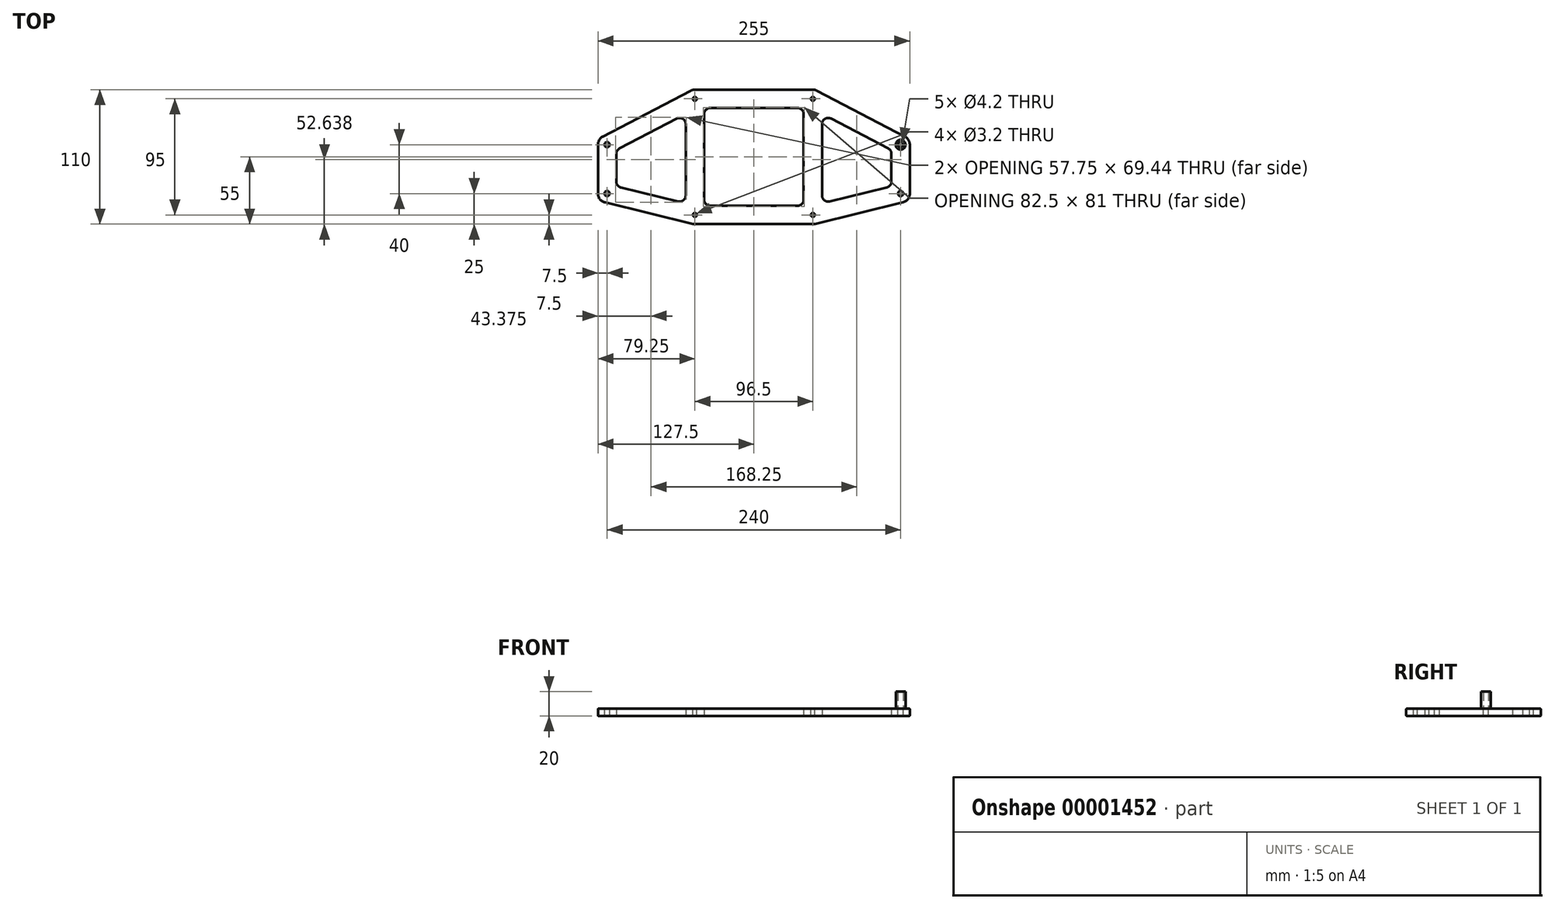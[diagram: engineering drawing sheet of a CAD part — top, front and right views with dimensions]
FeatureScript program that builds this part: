
annotation { "Feature Type Name" : "Feature", "Feature Type Description" : "" }
export const myFeature = defineFeature(function(context is Context, id is Id, definition is map)
    precondition{}
    {
        {
            var Q0;
            Q0=qCreatedBy(makeId("Top.planeOp"),FACE);
            var sketch = newSketch(context, id + "F0", { "sketchPlane" : qUnion([Q0])});
            skLineSegment(sketch, "E0.rect.bottom", {"start": v(120, 20) * mm, "end": v(-120, 20) * mm, "construction": true});
            skLineSegment(sketch, "E0.rect.top", {"start": v(120, -20) * mm, "end": v(-120, -20) * mm, "construction": true});
            skLineSegment(sketch, "E0.rect.left", {"start": v(120, 20) * mm, "end": v(120, -20) * mm, "construction": true});
            skLineSegment(sketch, "E0.rect.right", {"start": v(-120, 20) * mm, "end": v(-120, -20) * mm, "construction": true});
            skPoint(sketch, "E0.rect.middle", {"position": v(0, 0) * mm});
            skLineSegment(sketch, "E1.rect.bottom", {"start": v(48.25, 57.5) * mm, "end": v(-48.25, 57.5) * mm, "construction": true});
            skLineSegment(sketch, "E1.rect.top", {"start": v(48.25, -37.5) * mm, "end": v(-48.25, -37.5) * mm, "construction": true});
            skLineSegment(sketch, "E1.rect.left", {"start": v(48.25, 57.5) * mm, "end": v(48.25, -37.5) * mm, "construction": true});
            skLineSegment(sketch, "E1.rect.right", {"start": v(-48.25, 57.5) * mm, "end": v(-48.25, -37.5) * mm, "construction": true});
            skPoint(sketch, "E1.rect.middle", {"position": v(0, 10) * mm});
            skLineSegment(sketch, "E2", {"start": v(-120, 20) * mm, "end": v(-48.25, 57.5) * mm, "construction": true});
            skLineSegment(sketch, "E3", {"start": v(48.25, 57.5) * mm, "end": v(120, 20) * mm, "construction": true});
            skLineSegment(sketch, "E4", {"start": v(120, -20) * mm, "end": v(48.25, -37.5) * mm, "construction": true});
            skLineSegment(sketch, "E5", {"start": v(-48.25, -37.5) * mm, "end": v(-120, -20) * mm, "construction": true});
            skLineSegment(sketch, "E6.0", {"start": v(-127.5, 24.54) * mm, "end": v(-127.5, -25.9) * mm});
            skLineSegment(sketch, "E6.1", {"start": v(-49.15, -45) * mm, "end": v(-127.5, -25.9) * mm});
            skLineSegment(sketch, "E6.2", {"start": v(49.15, -45) * mm, "end": v(-49.15, -45) * mm});
            skLineSegment(sketch, "E6.3", {"start": v(127.5, -25.9) * mm, "end": v(49.15, -45) * mm});
            skLineSegment(sketch, "E6.4", {"start": v(127.5, 24.54) * mm, "end": v(127.5, -25.9) * mm});
            skLineSegment(sketch, "E6.5", {"start": v(-127.5, 24.54) * mm, "end": v(-50.1, 65) * mm});
            skLineSegment(sketch, "E6.6", {"start": v(50.1, 65) * mm, "end": v(127.5, 24.54) * mm});
            skLineSegment(sketch, "E6.7", {"start": v(50.1, 65) * mm, "end": v(-50.1, 65) * mm});
            skLineSegment(sketch, "E7.0", {"start": v(-112.5, 15.46) * mm, "end": v(-55.75, 45.12) * mm});
            skLineSegment(sketch, "E7.1", {"start": v(-112.5, 15.46) * mm, "end": v(-112.5, -14.1) * mm});
            skLineSegment(sketch, "E7.2", {"start": v(-55.75, -27.95) * mm, "end": v(-112.5, -14.1) * mm});
            skLineSegment(sketch, "E7.3", {"start": v(-55.75, 45.12) * mm, "end": v(-55.75, -27.95) * mm});
            skLineSegment(sketch, "E8.0", {"start": v(-40.75, 50) * mm, "end": v(-40.75, -30) * mm});
            skLineSegment(sketch, "E8.1", {"start": v(40.75, 50) * mm, "end": v(-40.75, 50) * mm});
            skLineSegment(sketch, "E8.2", {"start": v(40.75, 50) * mm, "end": v(40.75, -30) * mm});
            skLineSegment(sketch, "E8.3", {"start": v(40.75, -30) * mm, "end": v(-40.75, -30) * mm});
            skLineSegment(sketch, "E9.0", {"start": v(55.75, 45.12) * mm, "end": v(112.5, 15.46) * mm});
            skLineSegment(sketch, "E9.1", {"start": v(55.75, 45.12) * mm, "end": v(55.75, -27.95) * mm});
            skLineSegment(sketch, "E9.2", {"start": v(112.5, -14.1) * mm, "end": v(55.75, -27.95) * mm});
            skLineSegment(sketch, "E9.3", {"start": v(112.5, 15.46) * mm, "end": v(112.5, -14.1) * mm});
            skSolve(sketch);
        }
        {
            var Q0;
            Q0=makeQuery(id+"F0.imprint","IMPRINT",FACE,{"disambiguationData":[TD([[makeQuery(id+"F0.imprint","IMPRINT",EDGE,{"derivedFrom":sQuery(id+"F0.wireOp",EDGE,"E6.0")}),1.0]])]});
            extrude(context, id + "F1", {"entities" : qUnion([Q0]), "depth" : 6 * mm});
        }
        {
            var Q0;
            Q0=makeQuery(id+"F1.opExtrude","SWEPT_EDGE",EDGE,{"disambiguationData":[OSD([sQuery(id+"F0.wireOp",EDGE,"E6.0"),sQuery(id+"F0.wireOp",EDGE,"E6.1")])]});
            var Q1;
            Q1=makeQuery(id+"F1.opExtrude","SWEPT_EDGE",EDGE,{"disambiguationData":[OSD([sQuery(id+"F0.wireOp",EDGE,"E6.0"),sQuery(id+"F0.wireOp",EDGE,"E6.5")])]});
            var Q2;
            Q2=makeQuery(id+"F1.opExtrude","SWEPT_EDGE",EDGE,{"disambiguationData":[OSD([sQuery(id+"F0.wireOp",EDGE,"E6.1"),sQuery(id+"F0.wireOp",EDGE,"E6.2")])]});
            var Q3;
            Q3=makeQuery(id+"F1.opExtrude","SWEPT_EDGE",EDGE,{"disambiguationData":[OSD([sQuery(id+"F0.wireOp",EDGE,"E6.2"),sQuery(id+"F0.wireOp",EDGE,"E6.3")])]});
            var Q4;
            Q4=makeQuery(id+"F1.opExtrude","SWEPT_EDGE",EDGE,{"disambiguationData":[OSD([sQuery(id+"F0.wireOp",EDGE,"E6.3"),sQuery(id+"F0.wireOp",EDGE,"E6.4")])]});
            var Q5;
            Q5=makeQuery(id+"F1.opExtrude","SWEPT_EDGE",EDGE,{"disambiguationData":[OSD([sQuery(id+"F0.wireOp",EDGE,"E6.4"),sQuery(id+"F0.wireOp",EDGE,"E6.6")])]});
            var Q6;
            Q6=makeQuery(id+"F1.opExtrude","SWEPT_EDGE",EDGE,{"disambiguationData":[OSD([sQuery(id+"F0.wireOp",EDGE,"E6.6"),sQuery(id+"F0.wireOp",EDGE,"E6.7")])]});
            var Q7;
            Q7=makeQuery(id+"F1.opExtrude","SWEPT_EDGE",EDGE,{"disambiguationData":[OSD([sQuery(id+"F0.wireOp",EDGE,"E6.5"),sQuery(id+"F0.wireOp",EDGE,"E6.7")])]});
            fillet(context, id + "F2", {"entities" : qUnion([Q0, Q1, Q2, Q3, Q4, Q5, Q6, Q7]), "radius" : 7.5 * mm, "tangentPropagation" : true, "allowEdgeOverflow" : false});
        }
        {
            var Q0;
            Q0=makeQuery(id+"F1.opExtrude","SWEPT_EDGE",EDGE,{"disambiguationData":[OSD([sQuery(id+"F0.wireOp",EDGE,"E7.0"),sQuery(id+"F0.wireOp",EDGE,"E7.1")])]});
            var Q1;
            Q1=makeQuery(id+"F1.opExtrude","SWEPT_EDGE",EDGE,{"disambiguationData":[OSD([sQuery(id+"F0.wireOp",EDGE,"E7.1"),sQuery(id+"F0.wireOp",EDGE,"E7.2")])]});
            var Q2;
            Q2=makeQuery(id+"F1.opExtrude","SWEPT_EDGE",EDGE,{"disambiguationData":[OSD([sQuery(id+"F0.wireOp",EDGE,"E7.2"),sQuery(id+"F0.wireOp",EDGE,"E7.3")])]});
            var Q3;
            Q3=makeQuery(id+"F1.opExtrude","SWEPT_EDGE",EDGE,{"disambiguationData":[OSD([sQuery(id+"F0.wireOp",EDGE,"E7.0"),sQuery(id+"F0.wireOp",EDGE,"E7.3")])]});
            var Q4;
            Q4=makeQuery(id+"F1.opExtrude","SWEPT_EDGE",EDGE,{"disambiguationData":[OSD([sQuery(id+"F0.wireOp",EDGE,"E8.0"),sQuery(id+"F0.wireOp",EDGE,"E8.1")])]});
            var Q5;
            Q5=makeQuery(id+"F1.opExtrude","SWEPT_EDGE",EDGE,{"disambiguationData":[OSD([sQuery(id+"F0.wireOp",EDGE,"E8.0"),sQuery(id+"F0.wireOp",EDGE,"E8.3")])]});
            var Q6;
            Q6=makeQuery(id+"F1.opExtrude","SWEPT_EDGE",EDGE,{"disambiguationData":[OSD([sQuery(id+"F0.wireOp",EDGE,"E8.2"),sQuery(id+"F0.wireOp",EDGE,"E8.3")])]});
            var Q7;
            Q7=makeQuery(id+"F1.opExtrude","SWEPT_EDGE",EDGE,{"disambiguationData":[OSD([sQuery(id+"F0.wireOp",EDGE,"E8.1"),sQuery(id+"F0.wireOp",EDGE,"E8.2")])]});
            var Q8;
            Q8=makeQuery(id+"F1.opExtrude","SWEPT_EDGE",EDGE,{"disambiguationData":[OSD([sQuery(id+"F0.wireOp",EDGE,"E9.1"),sQuery(id+"F0.wireOp",EDGE,"E9.2")])]});
            var Q9;
            Q9=makeQuery(id+"F1.opExtrude","SWEPT_EDGE",EDGE,{"disambiguationData":[OSD([sQuery(id+"F0.wireOp",EDGE,"E9.0"),sQuery(id+"F0.wireOp",EDGE,"E9.3")])]});
            var Q10;
            Q10=makeQuery(id+"F1.opExtrude","SWEPT_EDGE",EDGE,{"disambiguationData":[OSD([sQuery(id+"F0.wireOp",EDGE,"E9.2"),sQuery(id+"F0.wireOp",EDGE,"E9.3")])]});
            var Q11;
            Q11=makeQuery(id+"F1.opExtrude","SWEPT_EDGE",EDGE,{"disambiguationData":[OSD([sQuery(id+"F0.wireOp",EDGE,"E9.0"),sQuery(id+"F0.wireOp",EDGE,"E9.1")])]});
            fillet(context, id + "F3", {"entities" : qUnion([Q0, Q1, Q2, Q3, Q4, Q5, Q6, Q7, Q8, Q9, Q10, Q11]), "radius" : 5 * mm, "tangentPropagation" : true, "allowEdgeOverflow" : false});
        }
        {
            var Q0;
            Q0=makeQuery(id+"F1.opExtrude","CAP_FACE",FACE,{"disambiguationData":[OSD([sQuery(id+"F0.wireOp",EDGE,"E6.0"),sQuery(id+"F0.wireOp",EDGE,"E6.1"),sQuery(id+"F0.wireOp",EDGE,"E6.2"),sQuery(id+"F0.wireOp",EDGE,"E6.3"),sQuery(id+"F0.wireOp",EDGE,"E6.4"),sQuery(id+"F0.wireOp",EDGE,"E6.5"),sQuery(id+"F0.wireOp",EDGE,"E6.6"),sQuery(id+"F0.wireOp",EDGE,"E6.7"),sQuery(id+"F0.wireOp",EDGE,"E7.0"),sQuery(id+"F0.wireOp",EDGE,"E7.1"),sQuery(id+"F0.wireOp",EDGE,"E7.2"),sQuery(id+"F0.wireOp",EDGE,"E7.3"),sQuery(id+"F0.wireOp",EDGE,"E8.0"),sQuery(id+"F0.wireOp",EDGE,"E8.1"),sQuery(id+"F0.wireOp",EDGE,"E8.2"),sQuery(id+"F0.wireOp",EDGE,"E8.3"),sQuery(id+"F0.wireOp",EDGE,"E9.0"),sQuery(id+"F0.wireOp",EDGE,"E9.1"),sQuery(id+"F0.wireOp",EDGE,"E9.2"),sQuery(id+"F0.wireOp",EDGE,"E9.3")])],"isStart":false});
            var Q1;
            Q1=makeQuery(id+"F1.opExtrude","CAP_FACE",FACE,{"disambiguationData":[OSD([sQuery(id+"F0.wireOp",EDGE,"E6.0"),sQuery(id+"F0.wireOp",EDGE,"E6.1"),sQuery(id+"F0.wireOp",EDGE,"E6.2"),sQuery(id+"F0.wireOp",EDGE,"E6.3"),sQuery(id+"F0.wireOp",EDGE,"E6.4"),sQuery(id+"F0.wireOp",EDGE,"E6.5"),sQuery(id+"F0.wireOp",EDGE,"E6.6"),sQuery(id+"F0.wireOp",EDGE,"E6.7"),sQuery(id+"F0.wireOp",EDGE,"E7.0"),sQuery(id+"F0.wireOp",EDGE,"E7.1"),sQuery(id+"F0.wireOp",EDGE,"E7.2"),sQuery(id+"F0.wireOp",EDGE,"E7.3"),sQuery(id+"F0.wireOp",EDGE,"E8.0"),sQuery(id+"F0.wireOp",EDGE,"E8.1"),sQuery(id+"F0.wireOp",EDGE,"E8.2"),sQuery(id+"F0.wireOp",EDGE,"E8.3"),sQuery(id+"F0.wireOp",EDGE,"E9.0"),sQuery(id+"F0.wireOp",EDGE,"E9.1"),sQuery(id+"F0.wireOp",EDGE,"E9.2"),sQuery(id+"F0.wireOp",EDGE,"E9.3")])],"isStart":true});
            fillet(context, id + "F4", {"entities" : qUnion([Q0, Q1]), "radius" : .5 * mm, "tangentPropagation" : true, "allowEdgeOverflow" : false});
        }
        {
            var Q0;
            Q0=makeQuery(id+"F1.opExtrude","CAP_FACE",FACE,{"disambiguationData":[OSD([sQuery(id+"F0.wireOp",EDGE,"E6.0"),sQuery(id+"F0.wireOp",EDGE,"E6.1"),sQuery(id+"F0.wireOp",EDGE,"E6.2"),sQuery(id+"F0.wireOp",EDGE,"E6.3"),sQuery(id+"F0.wireOp",EDGE,"E6.4"),sQuery(id+"F0.wireOp",EDGE,"E6.5"),sQuery(id+"F0.wireOp",EDGE,"E6.6"),sQuery(id+"F0.wireOp",EDGE,"E6.7"),sQuery(id+"F0.wireOp",EDGE,"E7.0"),sQuery(id+"F0.wireOp",EDGE,"E7.1"),sQuery(id+"F0.wireOp",EDGE,"E7.2"),sQuery(id+"F0.wireOp",EDGE,"E7.3"),sQuery(id+"F0.wireOp",EDGE,"E8.0"),sQuery(id+"F0.wireOp",EDGE,"E8.1"),sQuery(id+"F0.wireOp",EDGE,"E8.2"),sQuery(id+"F0.wireOp",EDGE,"E8.3"),sQuery(id+"F0.wireOp",EDGE,"E9.0"),sQuery(id+"F0.wireOp",EDGE,"E9.1"),sQuery(id+"F0.wireOp",EDGE,"E9.2"),sQuery(id+"F0.wireOp",EDGE,"E9.3")])],"isStart":false});
            var sketch = newSketch(context, id + "F5", { "sketchPlane" : qUnion([Q0])});
            skLineSegment(sketch, "E10.rect.bottom", {"start": v(120, 20) * mm, "end": v(-120, 20) * mm, "construction": true});
            skLineSegment(sketch, "E10.rect.top", {"start": v(120, -20) * mm, "end": v(-120, -20) * mm, "construction": true});
            skLineSegment(sketch, "E10.rect.left", {"start": v(120, 20) * mm, "end": v(120, -20) * mm, "construction": true});
            skLineSegment(sketch, "E10.rect.right", {"start": v(-120, 20) * mm, "end": v(-120, -20) * mm, "construction": true});
            skPoint(sketch, "E10.rect.middle", {"position": v(0, 0) * mm});
            skLineSegment(sketch, "E11.rect.bottom", {"start": v(-48.25, 57.5) * mm, "end": v(48.25, 57.5) * mm, "construction": true});
            skLineSegment(sketch, "E11.rect.top", {"start": v(-48.25, -37.5) * mm, "end": v(48.25, -37.5) * mm, "construction": true});
            skLineSegment(sketch, "E11.rect.left", {"start": v(-48.25, 57.5) * mm, "end": v(-48.25, -37.5) * mm, "construction": true});
            skLineSegment(sketch, "E11.rect.right", {"start": v(48.25, 57.5) * mm, "end": v(48.25, -37.5) * mm, "construction": true});
            skPoint(sketch, "E11.rect.middle", {"position": v(0, 10) * mm});
            skCircle(sketch, "E12", {"center": v(-120, 20) * mm, "radius": 2.1 * mm});
            skCircle(sketch, "E13", {"center": v(-48.25, 57.5) * mm, "radius": 1.6 * mm});
            skCircle(sketch, "E14", {"center": v(48.25, 57.5) * mm, "radius": 1.6 * mm});
            skCircle(sketch, "E15", {"center": v(120, 20) * mm, "radius": 2.1 * mm});
            skCircle(sketch, "E16", {"center": v(120, -20) * mm, "radius": 2.1 * mm});
            skCircle(sketch, "E17", {"center": v(48.25, -37.5) * mm, "radius": 1.6 * mm});
            skCircle(sketch, "E18", {"center": v(-48.25, -37.5) * mm, "radius": 1.6 * mm});
            skCircle(sketch, "E19", {"center": v(-120, -20) * mm, "radius": 2.1 * mm});
            skSolve(sketch);
        }
        {
            var Q0;
            {Q0=qUnion([makeQuery(id+"F5.imprint","IMPRINT",FACE,{"disambiguationData":[TD([[makeQuery(id+"F5.imprint","IMPRINT",EDGE,{"derivedFrom":sQuery(id+"F5.wireOp",EDGE,"E12")}),1.0]])]}),makeQuery(id+"F5.imprint","IMPRINT",FACE,{"disambiguationData":[TD([[makeQuery(id+"F5.imprint","IMPRINT",EDGE,{"derivedFrom":sQuery(id+"F5.wireOp",EDGE,"E13")}),1.0]])]}),makeQuery(id+"F5.imprint","IMPRINT",FACE,{"disambiguationData":[TD([[makeQuery(id+"F5.imprint","IMPRINT",EDGE,{"derivedFrom":sQuery(id+"F5.wireOp",EDGE,"E14")}),1.0]])]}),makeQuery(id+"F5.imprint","IMPRINT",FACE,{"disambiguationData":[TD([[makeQuery(id+"F5.imprint","IMPRINT",EDGE,{"derivedFrom":sQuery(id+"F5.wireOp",EDGE,"E15")}),1.0]])]}),makeQuery(id+"F5.imprint","IMPRINT",FACE,{"disambiguationData":[TD([[makeQuery(id+"F5.imprint","IMPRINT",EDGE,{"derivedFrom":sQuery(id+"F5.wireOp",EDGE,"E16")}),1.0]])]}),makeQuery(id+"F5.imprint","IMPRINT",FACE,{"disambiguationData":[TD([[makeQuery(id+"F5.imprint","IMPRINT",EDGE,{"derivedFrom":sQuery(id+"F5.wireOp",EDGE,"E17")}),1.0]])]}),makeQuery(id+"F5.imprint","IMPRINT",FACE,{"disambiguationData":[TD([[makeQuery(id+"F5.imprint","IMPRINT",EDGE,{"derivedFrom":sQuery(id+"F5.wireOp",EDGE,"E18")}),1.0]])]}),makeQuery(id+"F5.imprint","IMPRINT",FACE,{"disambiguationData":[TD([[makeQuery(id+"F5.imprint","IMPRINT",EDGE,{"derivedFrom":sQuery(id+"F5.wireOp",EDGE,"E19")}),1.0]])]})]);}
            extrude(context, id + "F6", {"entities" : qUnion([Q0]), "operationType" : NewBodyOperationType.REMOVE, "endBound" : BoundingType.THROUGH_ALL, "oppositeDirection" : true, "depth" : 25 * mm});
        }
        {
            var Q0;
            Q0=makeQuery(id+"F1.opExtrude","CAP_FACE",FACE,{"disambiguationData":[OSD([sQuery(id+"F0.wireOp",EDGE,"E6.0"),sQuery(id+"F0.wireOp",EDGE,"E6.1"),sQuery(id+"F0.wireOp",EDGE,"E6.2"),sQuery(id+"F0.wireOp",EDGE,"E6.3"),sQuery(id+"F0.wireOp",EDGE,"E6.4"),sQuery(id+"F0.wireOp",EDGE,"E6.5"),sQuery(id+"F0.wireOp",EDGE,"E6.6"),sQuery(id+"F0.wireOp",EDGE,"E6.7"),sQuery(id+"F0.wireOp",EDGE,"E7.0"),sQuery(id+"F0.wireOp",EDGE,"E7.1"),sQuery(id+"F0.wireOp",EDGE,"E7.2"),sQuery(id+"F0.wireOp",EDGE,"E7.3"),sQuery(id+"F0.wireOp",EDGE,"E8.0"),sQuery(id+"F0.wireOp",EDGE,"E8.1"),sQuery(id+"F0.wireOp",EDGE,"E8.2"),sQuery(id+"F0.wireOp",EDGE,"E8.3"),sQuery(id+"F0.wireOp",EDGE,"E9.0"),sQuery(id+"F0.wireOp",EDGE,"E9.1"),sQuery(id+"F0.wireOp",EDGE,"E9.2"),sQuery(id+"F0.wireOp",EDGE,"E9.3")])],"isStart":false});
            var sketch = newSketch(context, id + "F7", { "sketchPlane" : qUnion([Q0])});
            skCircle(sketch, "E20", {"center": v(120, 20) * mm, "radius": 4 * mm});
            skCircle(sketch, "E21", {"center": v(120, 20) * mm, "radius": 2.1 * mm});
            skSolve(sketch);
        }
        {
            var Q0;
            Q0=makeQuery(id+"F7.imprint","IMPRINT",FACE,{"disambiguationData":[TD([[makeQuery(id+"F7.imprint","IMPRINT",EDGE,{"derivedFrom":sQuery(id+"F7.wireOp",EDGE,"E20")}),1.0]])]});
            extrude(context, id + "F8", {"entities" : qUnion([Q0]), "depth" : 14 * mm});
        }
    });
